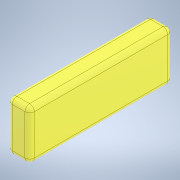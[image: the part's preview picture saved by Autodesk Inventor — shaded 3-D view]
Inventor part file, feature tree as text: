
AUTODESK INVENTOR PART (.ipt)
format: ipt  version: 2020.3 (Build 243373000, 373)  size: 118,272 bytes
history: native  units: mm
features: extrude x1, fillet x1, sketch x1
ambient origin geometry x8: Origin, YZ Plane, XZ Plane, XY Plane, X Axis, Y Axis, Z Axis, Center Point
bodies: Solid1 (feature_tree)
feature tree (3):
  extrude  "Extrusion1"  Depth=130.0mm
  fillet  "Fillet1"  Radius=45.0mm
  sketch  "Sketch1"  dims[d0=20.0mm d1=130.0mm d2=45.0mm d3=0.0mm d4=4.25mm]
